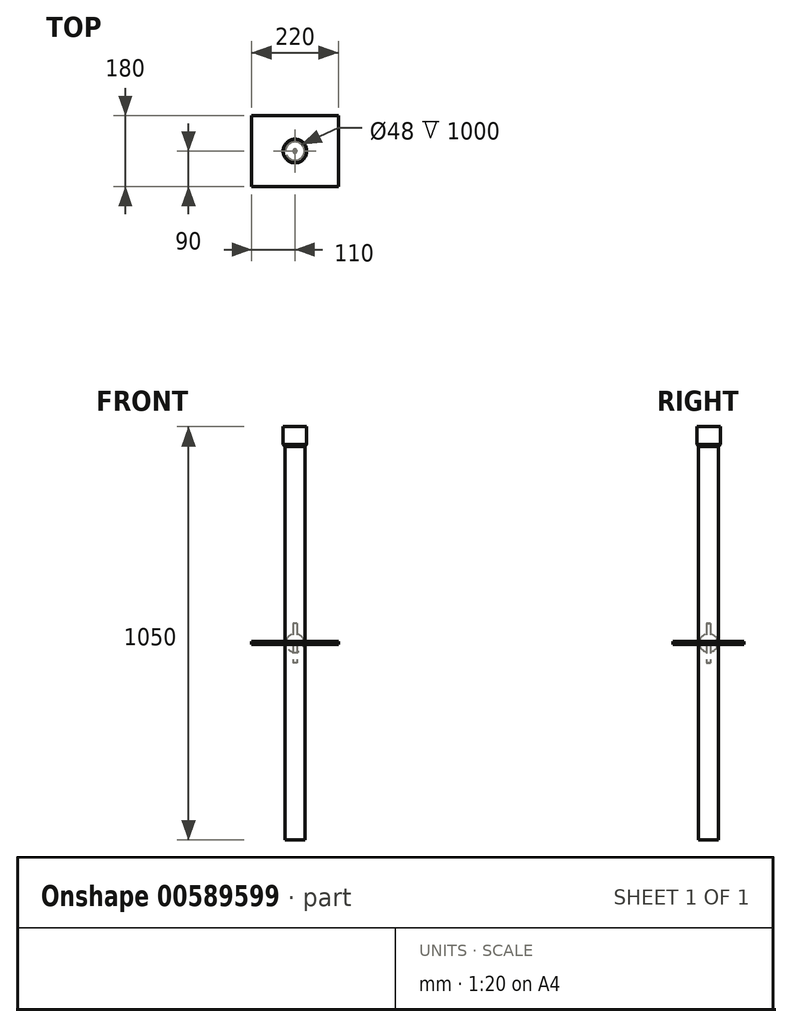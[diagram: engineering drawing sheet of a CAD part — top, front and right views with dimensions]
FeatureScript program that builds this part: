
annotation { "Feature Type Name" : "Feature", "Feature Type Description" : "" }
export const myFeature = defineFeature(function(context is Context, id is Id, definition is map)
    precondition{}
    {
        {
            var Q0;
            Q0=qCreatedBy(makeId("Top.planeOp"),FACE);
            var sketch = newSketch(context, id + "F0", { "sketchPlane" : qUnion([Q0])});
            skLineSegment(sketch, "E0.bottom", {"start": v(-110, 90) * mm, "end": v(110, 90) * mm});
            skLineSegment(sketch, "E0.top", {"start": v(-110, -90) * mm, "end": v(110, -90) * mm});
            skLineSegment(sketch, "E0.left", {"start": v(-110, 90) * mm, "end": v(-110, -90) * mm});
            skLineSegment(sketch, "E0.right", {"start": v(110, 90) * mm, "end": v(110, -90) * mm});
            skSolve(sketch);
        }
        {
            var Q0;
            Q0=makeQuery(id+"F0.imprint","IMPRINT",FACE,{"disambiguationData":[TD([[makeQuery(id+"F0.imprint","IMPRINT",EDGE,{"derivedFrom":sQuery(id+"F0.wireOp",EDGE,"E0.bottom")}),-1.0]])]});
            extrude(context, id + "F1", {"entities" : qUnion([Q0]), "depth" : 4 * mm, "offsetDistance" : 25 * mm, "hasSecondDirection" : true, "secondDirectionOppositeDirection" : true, "secondDirectionDepth" : 4 * mm});
        }
        {
            var Q0;
            Q0=qCreatedBy(makeId("Top.planeOp"),FACE);
            var sketch = newSketch(context, id + "F2", { "sketchPlane" : qUnion([Q0])});
            skCircle(sketch, "E1", {"center": v(0, 0) * mm, "radius": 5 * mm});
            skSolve(sketch);
        }
        {
            var Q0;
            Q0 = qSketchRegion(id + "F2", true);
            var Q1;
            Q1=makeQuery(id+"F2.imprint","IMPRINT",FACE,{"disambiguationData":[TD([[makeQuery(id+"F2.imprint","IMPRINT",EDGE,{"derivedFrom":sQuery(id+"F2.wireOp",EDGE,"E1")}),1.0]])]});
            extrude(context, id + "F3", {"entities" : qUnion([Q0, Q1]), "depth" : 50 * mm, "offsetDistance" : 25 * mm, "hasSecondDirection" : true, "secondDirectionOppositeDirection" : true, "secondDirectionDepth" : 50 * mm});
        }
        {
            var Q0;
            Q0=qCreatedBy(makeId("Top.planeOp"),FACE);
            var sketch = newSketch(context, id + "F4", { "sketchPlane" : qUnion([Q0])});
            skCircle(sketch, "E2", {"center": v(0, 0) * mm, "radius": 25.5 * mm});
            skCircle(sketch, "E3", {"center": v(0, 0) * mm, "radius": 24 * mm});
            skSolve(sketch);
        }
        {
            var Q0;
            Q0=makeQuery(id+"F4.imprint","IMPRINT",FACE,{"disambiguationData":[TD([[makeQuery(id+"F4.imprint","IMPRINT",EDGE,{"derivedFrom":sQuery(id+"F4.wireOp",EDGE,"E2")}),1.0]])]});
            extrude(context, id + "F5", {"entities" : qUnion([Q0]), "depth" : 500 * mm, "offsetDistance" : 25 * mm, "hasSecondDirection" : true, "secondDirectionOppositeDirection" : true, "secondDirectionDepth" : 500 * mm});
        }
        {
            var Q0;
            Q0=makeQuery(id+"F5.opExtrude","CAP_FACE",FACE,{"disambiguationData":[OSD([sQuery(id+"F4.wireOp",EDGE,"E2"),sQuery(id+"F4.wireOp",EDGE,"E3")])],"isStart":false});
            var sketch = newSketch(context, id + "F6", { "sketchPlane" : qUnion([Q0])});
            skCircle(sketch, "E4", {"center": v(0, 0) * mm, "radius": 30 * mm});
            skSolve(sketch);
        }
        {
            var Q0;
            Q0=makeQuery(id+"F6.imprint","IMPRINT",FACE,{"disambiguationData":[TD([[makeQuery(id+"F6.imprint","IMPRINT",EDGE,{"derivedFrom":sQuery(id+"F6.wireOp",EDGE,"E4")}),1.0]])]});
            var Q1;
            Q1=makeQuery(id+"F6.imprint","IMPRINT",FACE,{"disambiguationData":[TD([[makeQuery(id+"F6.imprint","IMPRINT",EDGE,{"derivedFrom":makeQuery(id+"F5.opExtrude","CAP_EDGE",EDGE,{"disambiguationData":[OSD([sQuery(id+"F4.wireOp",EDGE,"E3")])],"isStart":false})}),1.0]])]});
            var Q2;
            Q2=makeQuery(id+"F6.imprint","IMPRINT",FACE,{"disambiguationData":[TD([[makeQuery(id+"F6.imprint","IMPRINT",EDGE,{"derivedFrom":makeQuery(id+"F5.opExtrude","CAP_EDGE",EDGE,{"disambiguationData":[OSD([sQuery(id+"F4.wireOp",EDGE,"E2")])],"isStart":false})}),1.0]])]});
            extrude(context, id + "F7", {"entities" : qUnion([Q0, Q1, Q2]), "depth" : 50 * mm, "offsetDistance" : 25 * mm});
        }
        {
            var Q0;
            Q0=makeQuery(id+"F7.opExtrude","CAP_EDGE",EDGE,{"disambiguationData":[OSD([sQuery(id+"F6.wireOp",EDGE,"E4")])],"isStart":true});
            chamfer(context, id + "F8", {"entities" : qUnion([Q0]), "width" : 5 * mm, "tangentPropagation" : true});
        }
        {
            var Q0;
            Q0=qCreatedBy(makeId("Top.planeOp"),FACE);
            var sketch = newSketch(context, id + "F9", { "sketchPlane" : qUnion([Q0])});
            skArc(sketch, "E5", {"start": v(0, 23.5) * mm, "mid": v(-23.5, 0) * mm, "end": v(0, -23.5) * mm});
            skLineSegment(sketch, "E6", {"start": v(0, 0) * mm, "end": v(0, 23.5) * mm});
            skLineSegment(sketch, "E7", {"start": v(0, 23.5) * mm, "end": v(0, -23.5) * mm});
            skSolve(sketch);
        }
        {
            var Q0;
            {var subQ0=sQuery(id+"F9.wireOp",EDGE,"E5");Q0=makeQuery(id+"F9.imprint","IMPRINT",FACE,{"disambiguationData":[TD([[makeQuery(id+"F9.imprint","IMPRINT",EDGE,{"derivedFrom":subQ0}),1.0]])]});}
            var Q1;
            Q1=sQuery(id+"F9.wireOp",EDGE,"E7");
            revolve(context, id + "F10", {"entities" : qUnion([Q0]), "axis" : qUnion([Q1]), "revolveType" : RevolveType.FULL});
        }
    });
